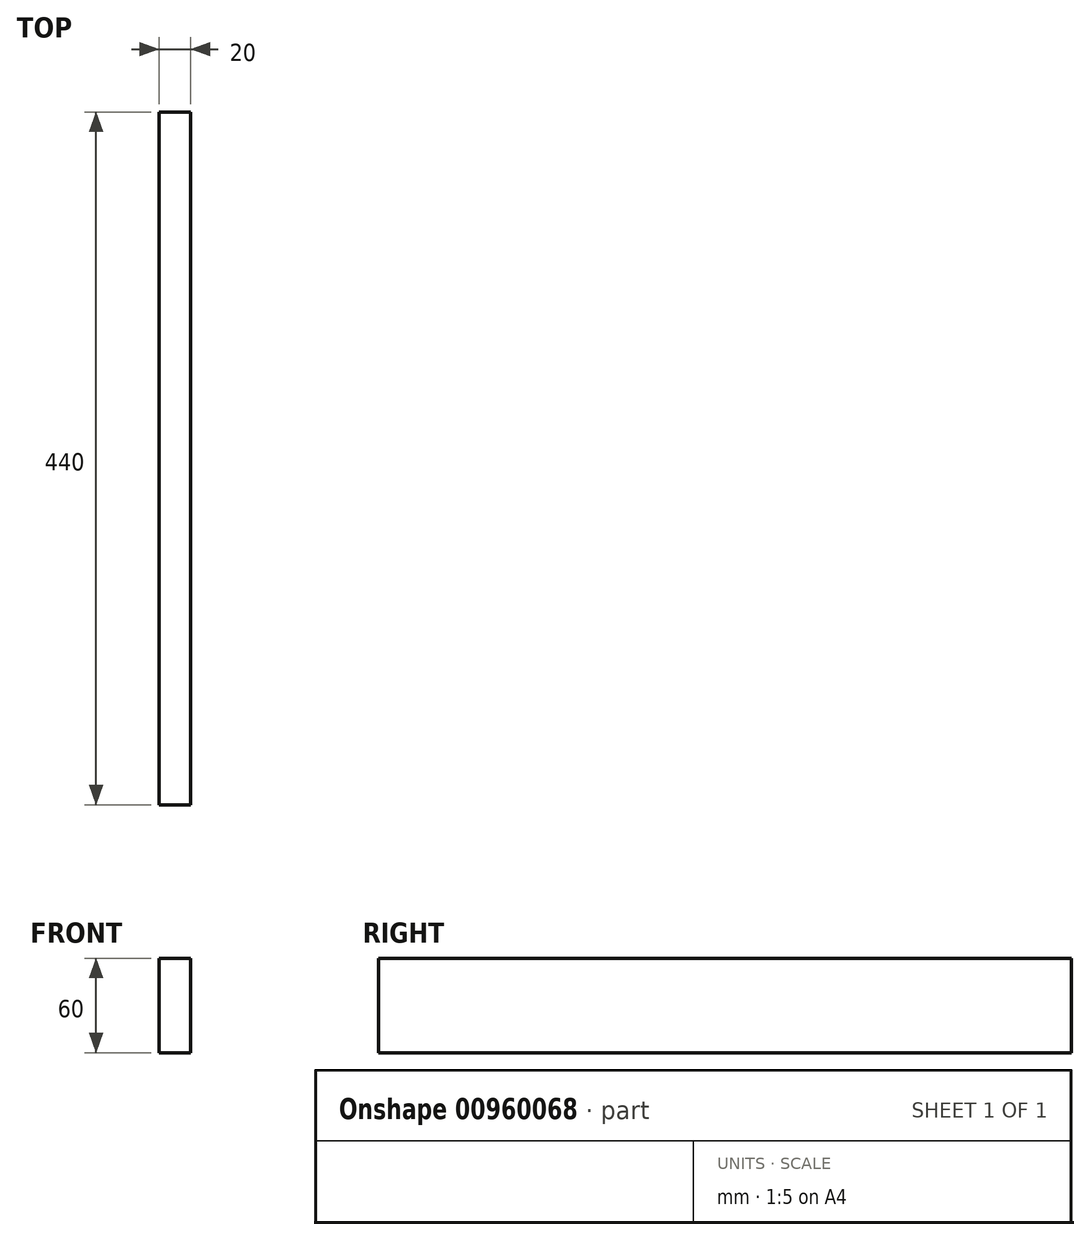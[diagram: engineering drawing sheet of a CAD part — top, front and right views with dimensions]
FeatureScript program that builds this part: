
annotation { "Feature Type Name" : "Feature", "Feature Type Description" : "" }
export const myFeature = defineFeature(function(context is Context, id is Id, definition is map)
    precondition{}
    {
        {
            var Q0;
            Q0=qCreatedBy(makeId("Right.planeOp"),FACE);
            var sketch = newSketch(context, id + "F0", { "sketchPlane" : qUnion([Q0])});
            skLineSegment(sketch, "E0", {"start": v(-220, 0) * mm, "end": v(-220, -18) * mm});
            skLineSegment(sketch, "E1", {"start": v(-220, -52) * mm, "end": v(-220, -60) * mm});
            skLineSegment(sketch, "E2", {"start": v(-220, -60) * mm, "end": v(0, -60) * mm});
            skLineSegment(sketch, "E3", {"start": v(-220, 0) * mm, "end": v(0, 0) * mm});
            skLineSegment(sketch, "E4.MirrorCS", {"start": v(220, 0) * mm, "end": v(0, 0) * mm});
            skLineSegment(sketch, "E5.MirrorCS", {"start": v(220, 0) * mm, "end": v(220, -18) * mm});
            skLineSegment(sketch, "E6.MirrorCS", {"start": v(220, -52) * mm, "end": v(220, -60) * mm});
            skLineSegment(sketch, "E7.MirrorCS", {"start": v(220, -60) * mm, "end": v(0, -60) * mm});
            skLineSegment(sketch, "E8", {"start": v(-220, -18) * mm, "end": v(-220, -52) * mm});
            skLineSegment(sketch, "E9", {"start": v(220, -18) * mm, "end": v(220, -52) * mm});
            skSolve(sketch);
        }
        {
            var Q0;
            Q0=makeQuery(id+"F0.imprint","IMPRINT",FACE,{"disambiguationData":[TD([[makeQuery(id+"F0.imprint","IMPRINT",EDGE,{"derivedFrom":sQuery(id+"F0.wireOp",EDGE,"E0")}),1.0]])]});
            extrude(context, id + "F1", {"entities" : qUnion([Q0]), "depth" : 20 * mm, "offsetDistance" : 25 * mm});
        }
    });
